# Revit family: RA 8 DIXIT LED OSCILLANTE IP66
name_source: partatom
category: Lighting Fixtures
units: mm (PartAtom-declared; Revit-internal decimal feet)

## family parameters
Always vertical = Yes
Cut with Voids When Loaded = No
Host = Ceiling
Light Source = No
OmniClass Number = 23.80.70.11
OmniClass Title = Luminaries for Internal Lighting
Part Type = Normal
Room Calculation Point = No
Round Connector Dimension = Use Diameter
Shared = No

## types (1)
- RA 8 DIXIT LED OSCILLANTE IP66
    Body material = White Powder Coated Aluminium
    CRI L'indice di Resa Cromatica = 80
    Description = Gli incassi oscillanti RA 8 Dixit LED IP66 sono stati progettati per soddisfare le più diverse esigenze illuminotecniche, in particolare per l'applicazione in centri commerciali, negozi e uffici, anche in esterni.
L'elevato rendimento luminoso di RA 8 Dixit LED si coniuga con contenuti valori di luminanza e livelli di abbagliamento estremamente bassi, consentendo un ottimo comfort visivo.
Alto grado di protezione IP66. Driver incluso.
    Glass material = Glass
    Larghezza = 95 mm
    Manufacturer = ARIA
    Model = 235-250B-21
    Type = RA 8 body : RA 8 DIXIT LED OSCILLANTE IP66 1650lm 12W 3000K CRI80-65° WHITE
    Type Comments = Ceiling recessed light
    Type Image = RA8_DIXIT_LED_IP66_TAB-Sito-Ivela.jpg
    URL = https://www.aria.lighting
    body angle = 20.00°

## geometry (parser evidence)
native form markers: Sweep x3
no freeform markers — native parametric forms only
